# Revit family: On&On-Chair-Emeco
name_source: partatom
category: Furniture
revit_build: Autodesk Revit 2018 (Build: 20180423_1000(x64)
units: mm (PartAtom-declared; Revit-internal decimal feet)

## family parameters
Always vertical = Yes
Cut with Voids When Loaded = No
Room Calculation Point = No
Shared = No
Work Plane-Based = No

## types (30) — shared parameters
Assembly Code = E2020200
Description = On&On-Chair-Emeco
Manufacturer = Emeco
URL = https://www.emeco.net

## per-type parameters (varying)
| type | Glide Material | Hole | No hole | Seat Material | Stool Frame Material |
| Atlantic Dark Blue rPET | RAL 5008 | Yes | No | RAL 5008 | RAL 5008 |
| Atlantic Dark Blue rPET with Ash Plywood Seat | RAL 5008 | No | Yes | Ash texture | RAL 5008 |
| Atlantic Dark Blue rPET with Dark Ash Plywood Seat | RAL 5008 | No | Yes | Dark ash | RAL 5008 |
| Atlantic Dark Blue rPET with Oak Plywood Seat | RAL 5008 | No | Yes | Oak texture | RAL 5008 |
| Atlantic Dark Blue rPET with Upholstered Seat | RAL 5008 | No | Yes | Atlantic dark blue | RAL 5008 |
| California Light Blue rPET | NCS S5010-B70G | Yes | No | NCS S5010-B70G | NCS S5010-B70G |
| California Light Blue rPET with Ash Plywood Seat | NCS S5010-B70G | No | Yes | Ash texture | NCS S5010-B70G |
| California Light Blue rPET with Dark Ash Plywood Seat | NCS S5010-B70G | No | Yes | Dark ash | NCS S5010-B70G |
| California Light Blue rPET with Oak Plywood Seat | NCS S5010-B70G | No | Yes | Oak texture | NCS S5010-B70G |
| California Light Blue rPET with Upholstered Seat | NCS S5010-B70G | No | Yes | California Light Blue | NCS S5010-B70G |
| Coral Orange rPET | NCS S2570-Y70R | Yes | No | NCS S2570-Y70R | NCS S2570-Y70R |
| Coral Orange rPET with Ash Plywood Seat | NCS S2570-Y70R | No | Yes | Ash texture | NCS S2570-Y70R |
| Coral Orange rPET with Dark Ash Plywood Seat | NCS S2570-Y70R | No | Yes | Dark ash | NCS S2570-Y70R |
| Coral Orange rPET with Oak Plywood Seat | NCS S2570-Y70R | No | Yes | Oak texture | NCS S2570-Y70R |
| Coral Orange rPET with Upholstered Seat | NCS S2570-Y70R | No | Yes | Coral Orange | NCS S2570-Y70R |
| Cypress Green rPET | RAL 6003 | Yes | No | RAL 6003 | RAL 6003 |
| Cypress Green rPET with Ash Plywood Seat | RAL 6003 | No | Yes | Ash texture | RAL 6003 |
| Cypress Green rPET with Dark Ash Plywood Seat | RAL 6003 | No | Yes | Dark ash | RAL 6003 |
| Cypress Green rPET with Oak Plywood Seat | RAL 6003 | No | Yes | Oak texture | RAL 6003 |
| Cypress Green rPET with Upholstered Seat | RAL 6003 | No | Yes | Cypress Green | RAL 6003 |
| Lava Black rPET | RAL 9017 | Yes | No | RAL 9017 | RAL 9017 |
| Lava Black rPET with Ash Plywood Seat | RAL 9017 | No | Yes | Ash texture | RAL 9017 |
| Lava Black rPET with Dark Ash Plywood Seat | RAL 9017 | No | Yes | Dark ash | RAL 9017 |
| Lava Black rPET with Oak Plywood Seat | RAL 9017 | No | Yes | Oak texture | RAL 9017 |
| Lava Black rPET with Upholstered Seat | RAL 9017 | No | Yes | Lava black | RAL 9017 |
| Stockholm White rPET | RAL 9002 | Yes | No | RAL 9002 | RAL 9002 |
| Stockholm White rPET with Ash Plywood Seat | RAL 9002 | No | Yes | Ash texture | RAL 9002 |
| Stockholm White rPET with Dark Ash Plywood Seat | RAL 9002 | No | Yes | Dark ash | RAL 9002 |
| Stockholm White rPET with Oak Plywood Seat | RAL 9002 | No | Yes | Oak texture | RAL 9002 |
| Stockholm White rPET with Upholstered Seat | RAL 9002 | No | Yes | Stockholm White | RAL 9002 |

## geometry (parser evidence)
native form markers: Sweep x3
no freeform markers — native parametric forms only
